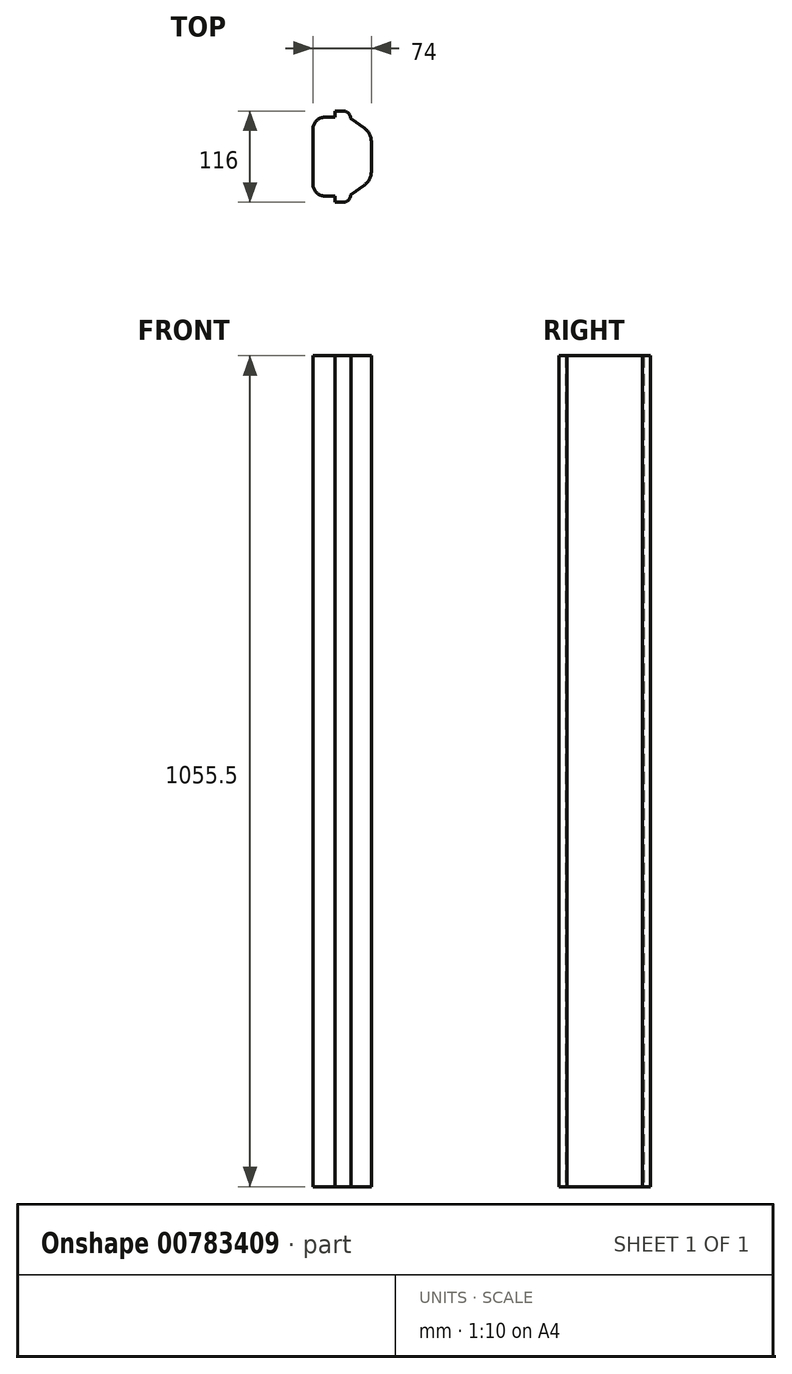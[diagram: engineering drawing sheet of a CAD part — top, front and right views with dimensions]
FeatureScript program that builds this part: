
annotation { "Feature Type Name" : "Feature", "Feature Type Description" : "" }
export const myFeature = defineFeature(function(context is Context, id is Id, definition is map)
    precondition{}
    {
        {
            var Q0;
            Q0=qCreatedBy(makeId("Top.planeOp"),FACE);
            var sketch = newSketch(context, id + "F0", { "sketchPlane" : qUnion([Q0])});
            skLineSegment(sketch, "E0", {"start": v(-413.58, -89.67) * mm, "end": v(460.15, -89.67) * mm, "construction": true});
            skLineSegment(sketch, "E1", {"start": v(239.27, -39.67) * mm, "end": v(252.27, -39.67) * mm});
            skArc(sketch, "E2.filletArc", {"start": v(239.27, -39.67) * mm, "mid": v(228.67, -44.06) * mm, "end": v(224.27, -54.67) * mm});
            skLineSegment(sketch, "E3", {"start": v(252.27, -39.67) * mm, "end": v(252.27, -31.67) * mm});
            skLineSegment(sketch, "E4", {"start": v(252.27, -31.67) * mm, "end": v(262.27, -31.67) * mm});
            skLineSegment(sketch, "E5.MirrorCS", {"start": v(252.27, -139.67) * mm, "end": v(252.27, -147.67) * mm});
            skLineSegment(sketch, "E6.MirrorCS", {"start": v(252.27, -147.67) * mm, "end": v(262.27, -147.67) * mm});
            skLineSegment(sketch, "E7.MirrorCS", {"start": v(239.27, -139.67) * mm, "end": v(252.27, -139.67) * mm});
            skArc(sketch, "E8.MirrorCS", {"start": v(239.27, -139.67) * mm, "mid": v(228.67, -135.28) * mm, "end": v(224.27, -124.67) * mm});
            skLineSegment(sketch, "E9", {"start": v(224.27, -124.67) * mm, "end": v(224.27, -54.67) * mm});
            skPoint(sketch, "E10.visualSharp", {"position": v(272.27, -31.67) * mm});
            skArc(sketch, "E10.filletArc", {"start": v(272.27, -41.67) * mm, "mid": v(269.35, -34.6) * mm, "end": v(262.27, -31.67) * mm});
            skPoint(sketch, "E11.visualSharp", {"position": v(272.27, -147.67) * mm});
            skArc(sketch, "E11.filletArc", {"start": v(262.27, -147.67) * mm, "mid": v(269.35, -144.74) * mm, "end": v(272.27, -137.67) * mm});
            skLineSegment(sketch, "E12.0", {"start": v(298.27, -70.15) * mm, "end": v(298.27, -109.2) * mm});
            skLineSegment(sketch, "E13", {"start": v(272.27, -41.67) * mm, "end": v(289.66, -53.7) * mm});
            skLineSegment(sketch, "E14", {"start": v(289.66, -125.63) * mm, "end": v(272.27, -137.67) * mm});
            skPoint(sketch, "E15.visualSharp", {"position": v(298.27, -59.67) * mm});
            skArc(sketch, "E15.filletArc", {"start": v(298.27, -70.15) * mm, "mid": v(296, -60.87) * mm, "end": v(289.66, -53.7) * mm});
            skPoint(sketch, "E16.visualSharp", {"position": v(298.27, -119.67) * mm});
            skArc(sketch, "E16.filletArc", {"start": v(289.66, -125.63) * mm, "mid": v(296, -118.47) * mm, "end": v(298.27, -109.2) * mm});
            skSolve(sketch);
        }
        {
            var Q0;
            Q0=makeQuery(id+"F0.imprint","IMPRINT",FACE,{"disambiguationData":[TD([[makeQuery(id+"F0.imprint","IMPRINT",EDGE,{"derivedFrom":sQuery(id+"F0.wireOp",EDGE,"E1")}),-1.0]])]});
            extrude(context, id + "F1", {"entities" : qUnion([Q0]), "depth" : 1055.5 * mm, "offsetDistance" : 25 * mm});
        }
    });
